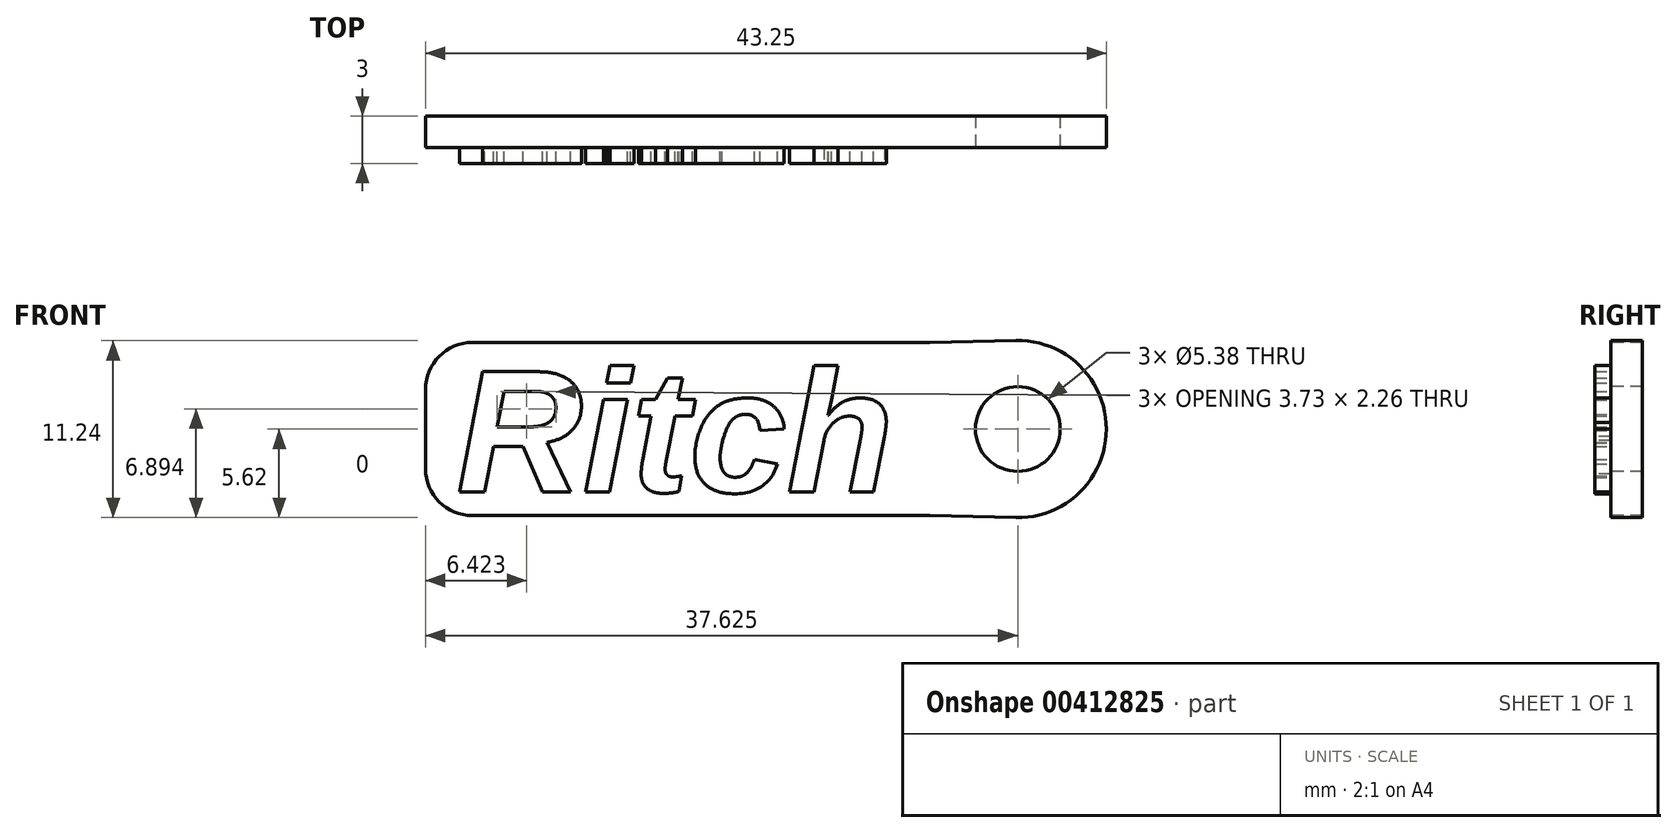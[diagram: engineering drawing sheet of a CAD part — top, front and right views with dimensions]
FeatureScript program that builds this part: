
annotation { "Feature Type Name" : "Feature", "Feature Type Description" : "" }
export const myFeature = defineFeature(function(context is Context, id is Id, definition is map)
    precondition{}
    {
        {
            var Q0;
            Q0=qCreatedBy(makeId("Front.planeOp"),FACE);
            var sketch = newSketch(context, id + "F0", { "sketchPlane" : qUnion([Q0])});
            skText(sketch, "E0", { "text": "Ritch", "fontName": "Arimo-BoldItalic.ttf"});
            const initialGuessF0  = {"E0": [-0.01404, -0.008, 1, 0, 0.008]};
            skSetInitialGuess(sketch, initialGuessF0);
            skSolve(sketch);
        }
        {
            var Q0;
            Q0=qSketchRegion(id+"F0",true);
            extrude(context, id + "F1", {"entities" : qUnion([Q0]), "depth" : 1 * mm});
        }
        {
            var Q0;
            Q0=qCreatedBy(makeId("Front.planeOp"),FACE);
            var sketch = newSketch(context, id + "F2", { "sketchPlane" : qUnion([Q0])});
            skLineSegment(sketch, "E1", {"start": v(16, -9.5) * mm, "end": v(-16, -9.5) * mm});
            skLineSegment(sketch, "E2", {"start": v(-16, 1.5) * mm, "end": v(16, 1.5) * mm});
            skLineSegment(sketch, "E3", {"start": v(16, -9.5) * mm, "end": v(16, 1.5) * mm, "construction": true});
            skLineSegment(sketch, "E4", {"start": v(-16, -9.5) * mm, "end": v(-16, 1.5) * mm});
            skCircle(sketch, "E5", {"center": v(21.62, -4) * mm, "radius": 5.62 * mm});
            skLineSegment(sketch, "E6", {"start": v(16, -4) * mm, "end": v(67.35, -4) * mm, "construction": true});
            skPoint(sketch, "E6.endSnap0", {"position": v(16, -4) * mm});
            skLineSegment(sketch, "E7", {"start": v(16, 1.5) * mm, "end": v(21.5, 1.62) * mm});
            skLineSegment(sketch, "E8", {"start": v(21.5, -9.62) * mm, "end": v(16, -9.5) * mm});
            skCircle(sketch, "E9", {"center": v(21.62, -4) * mm, "radius": 2.69 * mm});
            skSolve(sketch);
        }
        {
            var Q0;
            Q0=qSketchRegion(id+"F2",true);
            extrude(context, id + "F3", {"entities" : qUnion([Q0]), "oppositeDirection" : true, "depth" : 2 * mm});
        }
        {
            var Q0;
            Q0=makeQuery(id+"F3.opExtrude","SWEPT_EDGE",EDGE,{"disambiguationData":[OSD([sQuery(id+"F2.wireOp",EDGE,"E2"),sQuery(id+"F2.wireOp",EDGE,"E4")])]});
            var Q1;
            Q1=makeQuery(id+"F3.opExtrude","SWEPT_EDGE",EDGE,{"disambiguationData":[OSD([sQuery(id+"F2.wireOp",EDGE,"E1"),sQuery(id+"F2.wireOp",EDGE,"E4")])]});
            var Q2;
            Q2=makeQuery(id+"F3.opExtrude","SWEPT_EDGE",EDGE,{"disambiguationData":[OSD([sQuery(id+"F2.wireOp",EDGE,"E1"),sQuery(id+"F2.wireOp",EDGE,"E8")])]});
            var Q3;
            Q3=makeQuery(id+"F3.opExtrude","SWEPT_EDGE",EDGE,{"disambiguationData":[OSD([sQuery(id+"F2.wireOp",EDGE,"E2"),sQuery(id+"F2.wireOp",EDGE,"E7")])]});
            fillet(context, id + "F4", {"entities" : qUnion([Q0, Q1, Q2, Q3]), "radius" : 3 * mm, "tangentPropagation" : true, "allowEdgeOverflow" : false});
        }
    });
